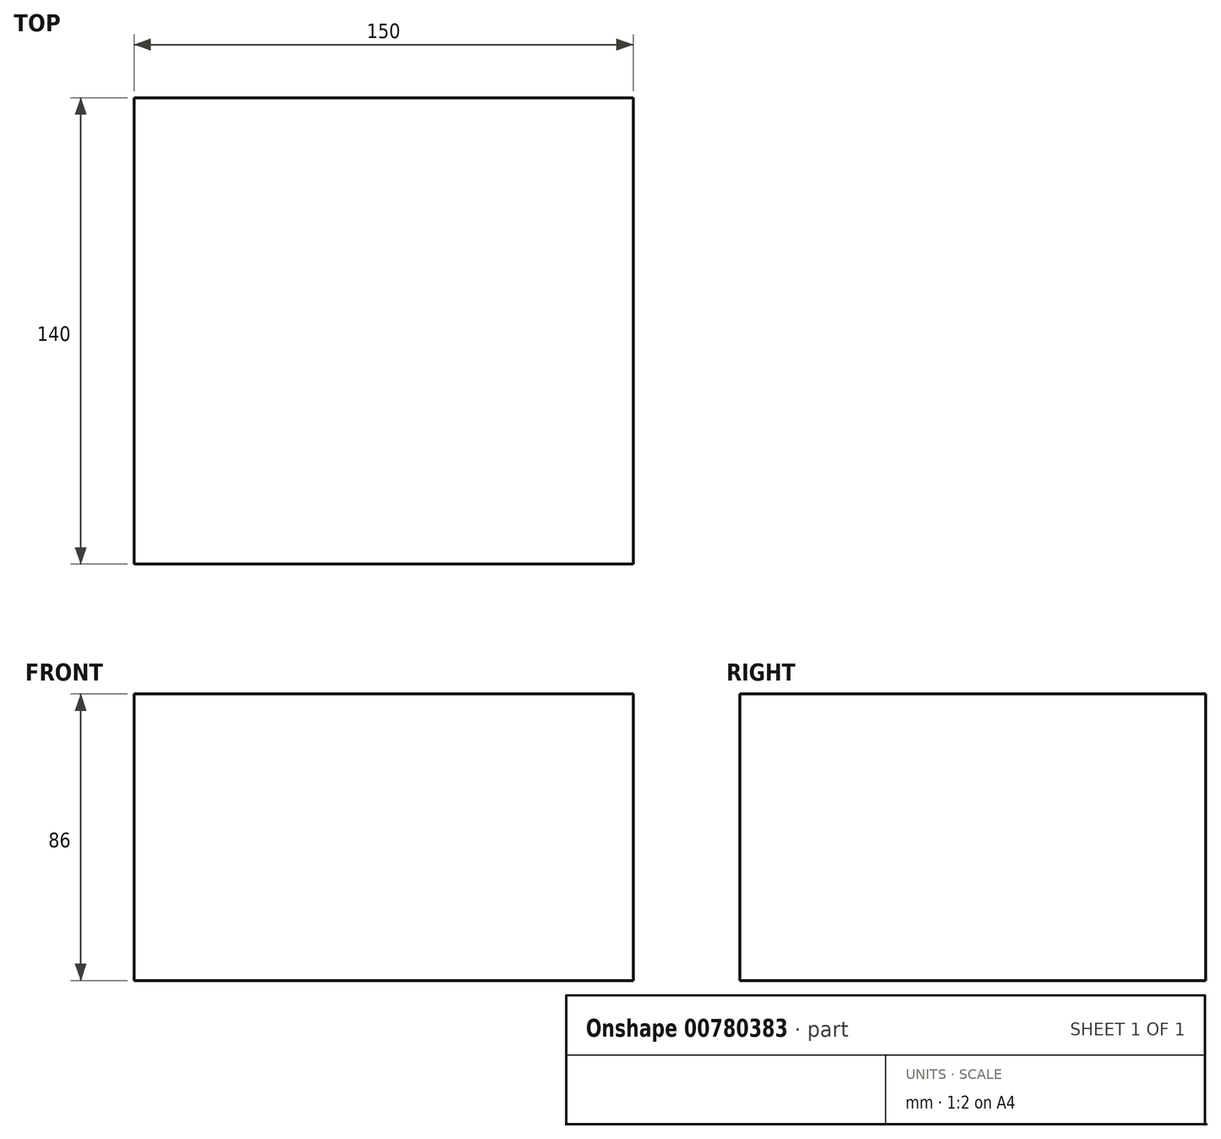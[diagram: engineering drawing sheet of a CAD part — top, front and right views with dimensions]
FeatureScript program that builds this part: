
annotation { "Feature Type Name" : "Feature", "Feature Type Description" : "" }
export const myFeature = defineFeature(function(context is Context, id is Id, definition is map)
    precondition{}
    {
        {
            var Q0;
            Q0=qCreatedBy(makeId("Top.planeOp"),FACE);
            var sketch = newSketch(context, id + "F0", { "sketchPlane" : qUnion([Q0])});
            skLineSegment(sketch, "E0.bottom", {"start": v(75, -70) * mm, "end": v(-75, -70) * mm});
            skLineSegment(sketch, "E0.top", {"start": v(75, 70) * mm, "end": v(-75, 70) * mm});
            skLineSegment(sketch, "E0.left", {"start": v(75, -70) * mm, "end": v(75, 70) * mm});
            skLineSegment(sketch, "E0.right", {"start": v(-75, -70) * mm, "end": v(-75, 70) * mm});
            skPoint(sketch, "E0.middle", {"position": v(0, 0) * mm});
            skSolve(sketch);
        }
        {
            var Q0;
            Q0=makeQuery(id+"F0.imprint","IMPRINT",FACE,{"disambiguationData":[TD([[makeQuery(id+"F0.imprint","IMPRINT",EDGE,{"derivedFrom":sQuery(id+"F0.wireOp",EDGE,"E0.bottom")}),-1.0]])]});
            extrude(context, id + "F1", {"entities" : qUnion([Q0]), "depth" : 86 * mm, "offsetDistance" : 25 * mm});
        }
    });
